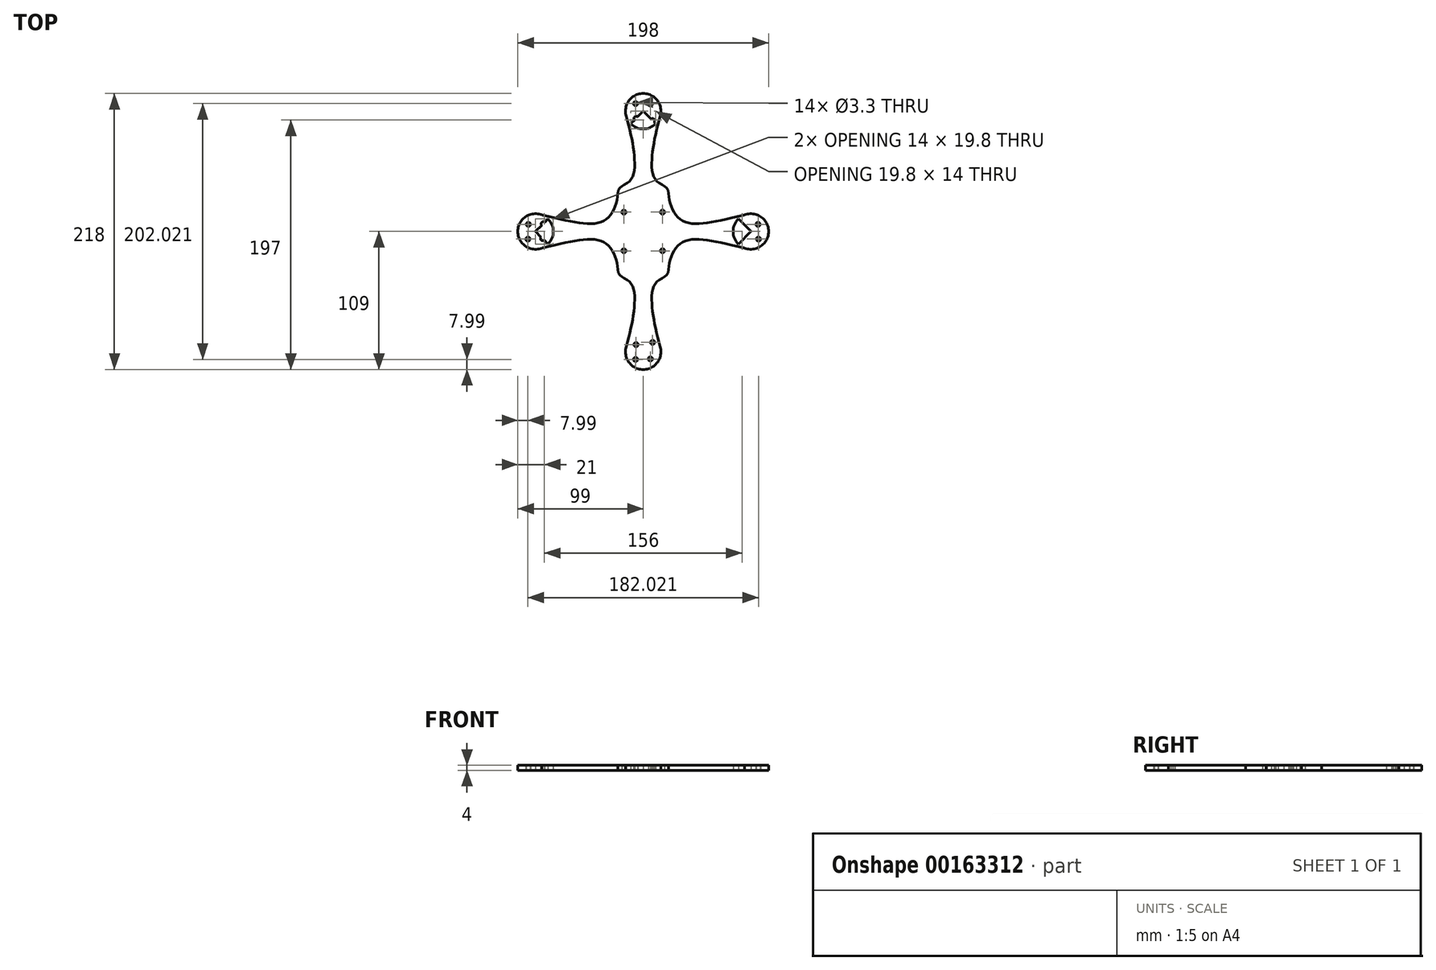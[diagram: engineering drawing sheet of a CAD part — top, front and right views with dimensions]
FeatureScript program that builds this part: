
annotation { "Feature Type Name" : "Feature", "Feature Type Description" : "" }
export const myFeature = defineFeature(function(context is Context, id is Id, definition is map)
    precondition{}
    {
        {
            var Q0;
            Q0=qCreatedBy(makeId("Top.planeOp"),FACE);
            var sketch = newSketch(context, id + "F0", { "sketchPlane" : qUnion([Q0])});
            skLineSegment(sketch, "E0", {"start": v(0, 394.6) * mm, "end": v(0, -405.4) * mm});
            skLineSegment(sketch, "E1", {"start": v(-497.38, 0) * mm, "end": v(616.02, 0) * mm});
            skCircle(sketch, "E2", {"center": v(0, -95) * mm, "radius": 14 * mm});
            skLineSegment(sketch, "E3", {"start": v(-9.9, -85.1) * mm, "end": v(0, -95) * mm});
            skLineSegment(sketch, "E4", {"start": v(0, -95) * mm, "end": v(9.9, -104.9) * mm});
            skLineSegment(sketch, "E5", {"start": v(0, -95) * mm, "end": v(9.9, -85.1) * mm});
            skLineSegment(sketch, "E6", {"start": v(0, -95) * mm, "end": v(-9.9, -104.9) * mm});
            skCircle(sketch, "E7", {"center": v(-6.01, -101.01) * mm, "radius": 1.65 * mm});
            skCircle(sketch, "E8", {"center": v(-5.66, -89.34) * mm, "radius": 1.65 * mm});
            skCircle(sketch, "E9", {"center": v(7.42, -87.58) * mm, "radius": 1.65 * mm});
            skCircle(sketch, "E10", {"center": v(5.66, -100.66) * mm, "radius": 1.65 * mm});
            skLineSegment(sketch, "E11.bottom", {"start": v(20, 30) * mm, "end": v(-20, 30) * mm});
            skLineSegment(sketch, "E11.top", {"start": v(20, -30) * mm, "end": v(-20, -30) * mm});
            skLineSegment(sketch, "E11.left", {"start": v(20, 30) * mm, "end": v(20, -30) * mm});
            skLineSegment(sketch, "E11.right", {"start": v(-20, 30) * mm, "end": v(-20, -30) * mm});
            skPoint(sketch, "E11.middle", {"position": v(0, 0) * mm});
            skCircle(sketch, "E12", {"center": v(-85, 0) * mm, "radius": 14 * mm});
            skLineSegment(sketch, "E13", {"start": v(-85, 0) * mm, "end": v(-68.46, 16.54) * mm});
            skLineSegment(sketch, "E14", {"start": v(-85, 0) * mm, "end": v(-96.5, -11.5) * mm});
            skLineSegment(sketch, "E15", {"start": v(-85, 0) * mm, "end": v(-98.46, 13.46) * mm});
            skLineSegment(sketch, "E16", {"start": v(-85, 0) * mm, "end": v(-73.1, -11.9) * mm});
            skCircle(sketch, "E17", {"center": v(-90.66, 5.66) * mm, "radius": 1.65 * mm});
            skCircle(sketch, "E18", {"center": v(-78.99, 6.01) * mm, "radius": 1.65 * mm});
            skCircle(sketch, "E19", {"center": v(-79.34, -5.66) * mm, "radius": 1.65 * mm});
            skCircle(sketch, "E20", {"center": v(-91.01, -6.01) * mm, "radius": 1.65 * mm});
            skCircle(sketch, "E21", {"center": v(-15.25, 15.25) * mm, "radius": 1.65 * mm});
            skCircle(sketch, "E22.MirrorC", {"center": v(15.25, 15.25) * mm, "radius": 1.65 * mm});
            skLineSegment(sketch, "E23.MirrorCS", {"start": v(85, 0) * mm, "end": v(98.46, 13.46) * mm});
            skCircle(sketch, "E24.MirrorC", {"center": v(79.34, -5.66) * mm, "radius": 1.65 * mm});
            skLineSegment(sketch, "E25.MirrorCS", {"start": v(85, 0) * mm, "end": v(96.5, -11.5) * mm});
            skCircle(sketch, "E26.MirrorC", {"center": v(78.99, 6.01) * mm, "radius": 1.65 * mm});
            skCircle(sketch, "E27.MirrorC", {"center": v(85, 0) * mm, "radius": 14 * mm});
            skLineSegment(sketch, "E28.MirrorCS", {"start": v(85, 0) * mm, "end": v(68.46, 16.54) * mm});
            skLineSegment(sketch, "E29.MirrorCS", {"start": v(85, 0) * mm, "end": v(73.1, -11.9) * mm});
            skCircle(sketch, "E30.MirrorC", {"center": v(91.01, -6.01) * mm, "radius": 1.65 * mm});
            skCircle(sketch, "E31.MirrorC", {"center": v(90.66, 5.66) * mm, "radius": 1.65 * mm});
            skCircle(sketch, "E32.MirrorC", {"center": v(-15.25, -15.25) * mm, "radius": 1.65 * mm});
            skCircle(sketch, "E33.MirrorC", {"center": v(15.25, -15.25) * mm, "radius": 1.65 * mm});
            skCircle(sketch, "E34.MirrorC", {"center": v(0, 95) * mm, "radius": 14 * mm});
            skLineSegment(sketch, "E35.MirrorCS", {"start": v(-9.9, 85.1) * mm, "end": v(0, 95) * mm});
            skCircle(sketch, "E36.MirrorC", {"center": v(5.66, 100.66) * mm, "radius": 1.65 * mm});
            skCircle(sketch, "E37.MirrorC", {"center": v(7.42, 87.58) * mm, "radius": 1.65 * mm});
            skCircle(sketch, "E38.MirrorC", {"center": v(-5.66, 89.34) * mm, "radius": 1.65 * mm});
            skCircle(sketch, "E39.MirrorC", {"center": v(-6.01, 101.01) * mm, "radius": 1.65 * mm});
            skLineSegment(sketch, "E40.MirrorCS", {"start": v(0, 95) * mm, "end": v(-9.9, 104.9) * mm});
            skLineSegment(sketch, "E41.MirrorCS", {"start": v(0, 95) * mm, "end": v(9.9, 85.1) * mm});
            skLineSegment(sketch, "E42.MirrorCS", {"start": v(0, 95) * mm, "end": v(9.9, 104.9) * mm});
            skFitSpline(sketch, "E43", {"points": [v(-20, -30) * mm, v(-10.64, -39.9) * mm, v(-6.93, -58.02) * mm, v(-13.53, -91.41) * mm], "startDerivative": vector(-3.31, -64.42) * mm, "endDerivative": vector(-25.02, -87) * mm});
            skFitSpline(sketch, "E44", {"points": [v(-20, -30) * mm, v(-31.64, -8.27) * mm, v(-79.94, -13.05) * mm], "startDerivative": vector(-4.64, 64.25) * mm, "endDerivative": vector(-107.73, -23.92) * mm});
            skFitSpline(sketch, "E45.MirrorCS", {"points": [v(-20, 30) * mm, v(-31.64, 8.27) * mm, v(-79.94, 13.05) * mm], "startDerivative": vector(-4.64, -64.25) * mm, "endDerivative": vector(-107.73, 23.92) * mm});
            skFitSpline(sketch, "E46.MirrorCS", {"points": [v(-20, 30) * mm, v(-10.64, 39.9) * mm, v(-6.93, 58.02) * mm, v(-13.53, 91.41) * mm], "startDerivative": vector(-3.31, 64.42) * mm, "endDerivative": vector(-25.02, 87) * mm});
            skFitSpline(sketch, "E47.MirrorCS", {"points": [v(20, -30) * mm, v(10.64, -39.9) * mm, v(6.93, -58.02) * mm, v(13.53, -91.41) * mm], "startDerivative": vector(3.31, -64.42) * mm, "endDerivative": vector(25.02, -87) * mm});
            skFitSpline(sketch, "E48.MirrorCS", {"points": [v(20, -30) * mm, v(31.64, -8.27) * mm, v(79.94, -13.05) * mm], "startDerivative": vector(4.64, 64.25) * mm, "endDerivative": vector(107.73, -23.92) * mm});
            skFitSpline(sketch, "E49.MirrorCS", {"points": [v(20, 30) * mm, v(31.64, 8.27) * mm, v(79.94, 13.05) * mm], "startDerivative": vector(4.64, -64.25) * mm, "endDerivative": vector(107.73, 23.92) * mm});
            skFitSpline(sketch, "E50.MirrorCS", {"points": [v(20, 30) * mm, v(10.64, 39.9) * mm, v(6.93, 58.02) * mm, v(13.53, 91.41) * mm], "startDerivative": vector(3.31, 64.42) * mm, "endDerivative": vector(25.02, 87) * mm});
            skSolve(sketch);
        }
        {
            var Q0;
            Q0 = qSketchRegion(id + "F0", true);
            var Q1;
            {var subQ1=sQuery(id+"F0.wireOp",EDGE,"E1");var subQ5=sQuery(id+"F0.wireOp",EDGE,"E12");var subQ8=makeQuery(id+"F0.imprint","INTERSECT",VERTEX,{"disambiguationData":[OD(1.0)],"derivedFrom":[subQ1,subQ5]});Q1=makeQuery(id+"F0.imprint","IMPRINT",FACE,{"disambiguationData":[TD([[makeQuery(id+"F0.imprint","IMPRINT",EDGE,{"disambiguationData":[TD([[subQ8,-1.0]])],"derivedFrom":subQ5}),1.0]])]});}
            var Q2;
            {var subQ1=sQuery(id+"F0.wireOp",EDGE,"E1");var subQ5=sQuery(id+"F0.wireOp",EDGE,"E12");var subQ6=makeQuery(id+"F0.imprint","INTERSECT",VERTEX,{"disambiguationData":[OD(1.0)],"derivedFrom":[subQ1,subQ5]});Q2=makeQuery(id+"F0.imprint","IMPRINT",FACE,{"disambiguationData":[TD([[makeQuery(id+"F0.imprint","IMPRINT",EDGE,{"disambiguationData":[TD([[subQ6,1.0]])],"derivedFrom":subQ5}),1.0]])]});}
            var Q3;
            {var subQ0=sQuery(id+"F0.wireOp",EDGE,"E3");var subQ5=sQuery(id+"F0.wireOp",EDGE,"E2");var subQ7=makeQuery(id+"F0.imprint","INTERSECT",VERTEX,{"derivedFrom":[subQ5,subQ0]});Q3=makeQuery(id+"F0.imprint","IMPRINT",FACE,{"disambiguationData":[TD([[makeQuery(id+"F0.imprint","IMPRINT",EDGE,{"disambiguationData":[TD([[subQ7,1.0]])],"derivedFrom":subQ5}),1.0]])]});}
            var Q4;
            {var subQ0=sQuery(id+"F0.wireOp",EDGE,"E5");var subQ1=sQuery(id+"F0.wireOp",EDGE,"E2");var subQ2=makeQuery(id+"F0.imprint","INTERSECT",VERTEX,{"derivedFrom":[subQ1,subQ0]});Q4=makeQuery(id+"F0.imprint","IMPRINT",FACE,{"disambiguationData":[TD([[makeQuery(id+"F0.imprint","IMPRINT",EDGE,{"disambiguationData":[TD([[subQ2,-1.0]])],"derivedFrom":subQ1}),1.0]])]});}
            var Q5;
            {var subQ0=sQuery(id+"F0.wireOp",EDGE,"E29.MirrorCS");var subQ3=sQuery(id+"F0.wireOp",EDGE,"E24.MirrorC");var subQ4=makeQuery(id+"F0.imprint","INTERSECT",VERTEX,{"disambiguationData":[OD(0.0)],"derivedFrom":[subQ3,subQ0]});Q5=makeQuery(id+"F0.imprint","IMPRINT",FACE,{"disambiguationData":[TD([[makeQuery(id+"F0.imprint","IMPRINT",EDGE,{"disambiguationData":[TD([[subQ4,1.0]])],"derivedFrom":subQ3}),1.0]])]});}
            var Q6;
            {var subQ3=sQuery(id+"F0.wireOp",EDGE,"E28.MirrorCS");var subQ5=sQuery(id+"F0.wireOp",EDGE,"E26.MirrorC");var subQ6=makeQuery(id+"F0.imprint","INTERSECT",VERTEX,{"disambiguationData":[OD(0.0)],"derivedFrom":[subQ5,subQ3]});Q6=makeQuery(id+"F0.imprint","IMPRINT",FACE,{"disambiguationData":[TD([[makeQuery(id+"F0.imprint","IMPRINT",EDGE,{"disambiguationData":[TD([[subQ6,-1.0]])],"derivedFrom":subQ5}),1.0]])]});}
            var Q7;
            {var subQ0=sQuery(id+"F0.wireOp",EDGE,"E35.MirrorCS");var subQ5=sQuery(id+"F0.wireOp",EDGE,"E34.MirrorC");var subQ6=makeQuery(id+"F0.imprint","INTERSECT",VERTEX,{"derivedFrom":[subQ5,subQ0]});Q7=makeQuery(id+"F0.imprint","IMPRINT",FACE,{"disambiguationData":[TD([[makeQuery(id+"F0.imprint","IMPRINT",EDGE,{"disambiguationData":[TD([[subQ6,1.0]])],"derivedFrom":subQ5}),-1.0]])]});}
            var Q8;
            {var subQ0=sQuery(id+"F0.wireOp",EDGE,"E41.MirrorCS");var subQ5=sQuery(id+"F0.wireOp",EDGE,"E34.MirrorC");var subQ6=makeQuery(id+"F0.imprint","INTERSECT",VERTEX,{"derivedFrom":[subQ5,subQ0]});Q8=makeQuery(id+"F0.imprint","IMPRINT",FACE,{"disambiguationData":[TD([[makeQuery(id+"F0.imprint","IMPRINT",EDGE,{"disambiguationData":[TD([[subQ6,-1.0]])],"derivedFrom":subQ5}),-1.0]])]});}
            extrude(context, id + "F1", {"entities" : qUnion([Q0, Q1, Q2, Q3, Q4, Q5, Q6, Q7, Q8]), "depth" : 4 * mm});
        }
    });
